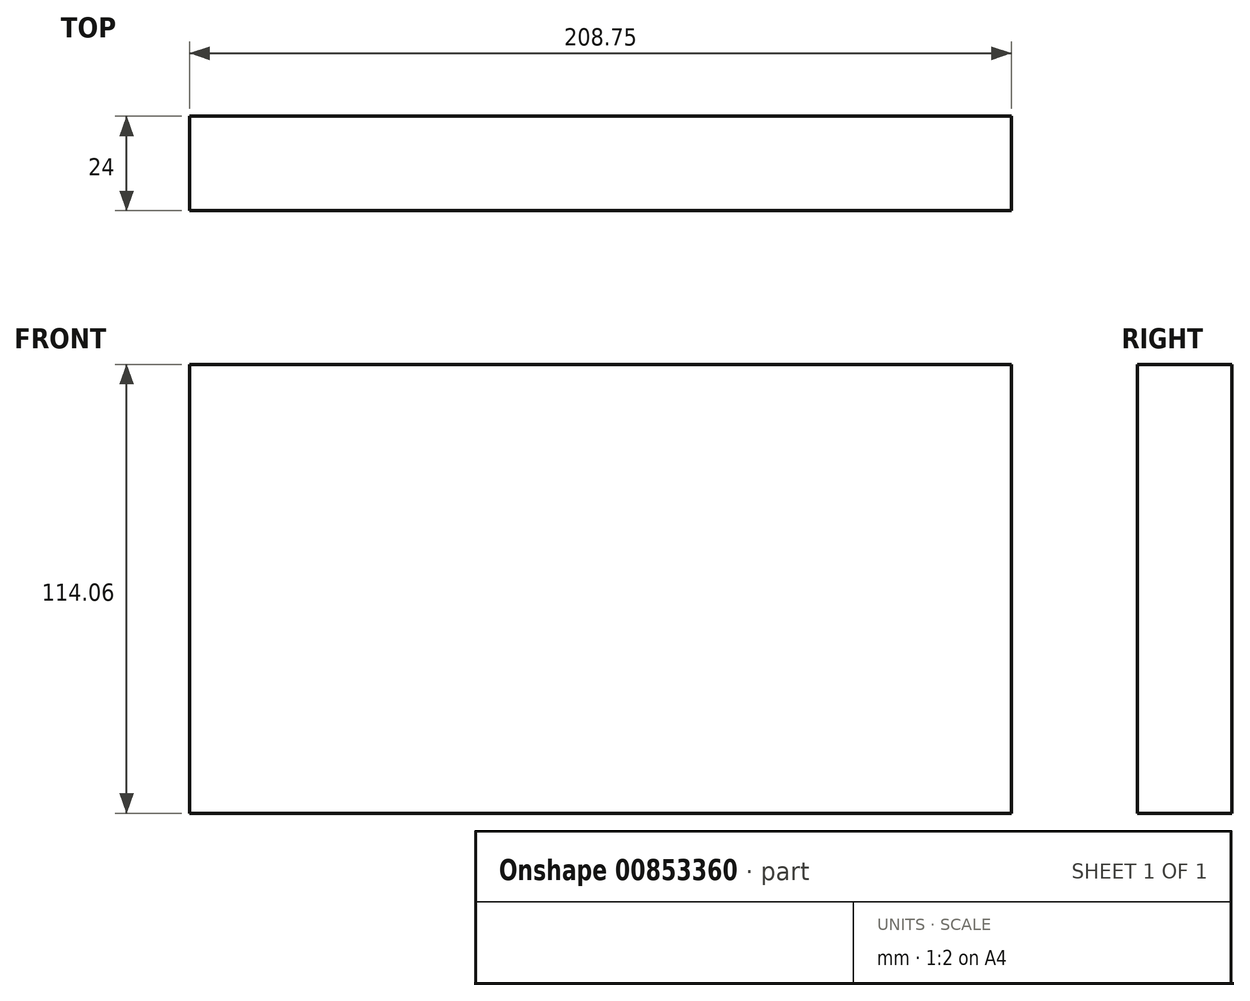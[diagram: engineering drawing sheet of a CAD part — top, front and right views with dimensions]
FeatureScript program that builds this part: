
annotation { "Feature Type Name" : "Feature", "Feature Type Description" : "" }
export const myFeature = defineFeature(function(context is Context, id is Id, definition is map)
    precondition{}
    {
        {
            var Q0;
            Q0=qCreatedBy(makeId("Front.planeOp"),FACE);
            var sketch = newSketch(context, id + "F0", { "sketchPlane" : qUnion([Q0])});
            skLineSegment(sketch, "E0.bottom", {"start": v(-120.78, 71.4) * mm, "end": v(87.97, 71.4) * mm});
            skLineSegment(sketch, "E0.top", {"start": v(-120.78, -42.67) * mm, "end": v(87.97, -42.67) * mm});
            skLineSegment(sketch, "E0.left", {"start": v(-120.78, 71.4) * mm, "end": v(-120.78, -42.67) * mm});
            skLineSegment(sketch, "E0.right", {"start": v(87.97, 71.4) * mm, "end": v(87.97, -42.67) * mm});
            skSolve(sketch);
        }
        {
            var Q0;
            Q0 = qSketchRegion(id + "F0", true);
            extrude(context, id + "F1", {"entities" : qUnion([Q0]), "depth" : 24 * mm, "offsetDistance" : 25.4 * mm});
        }
    });
